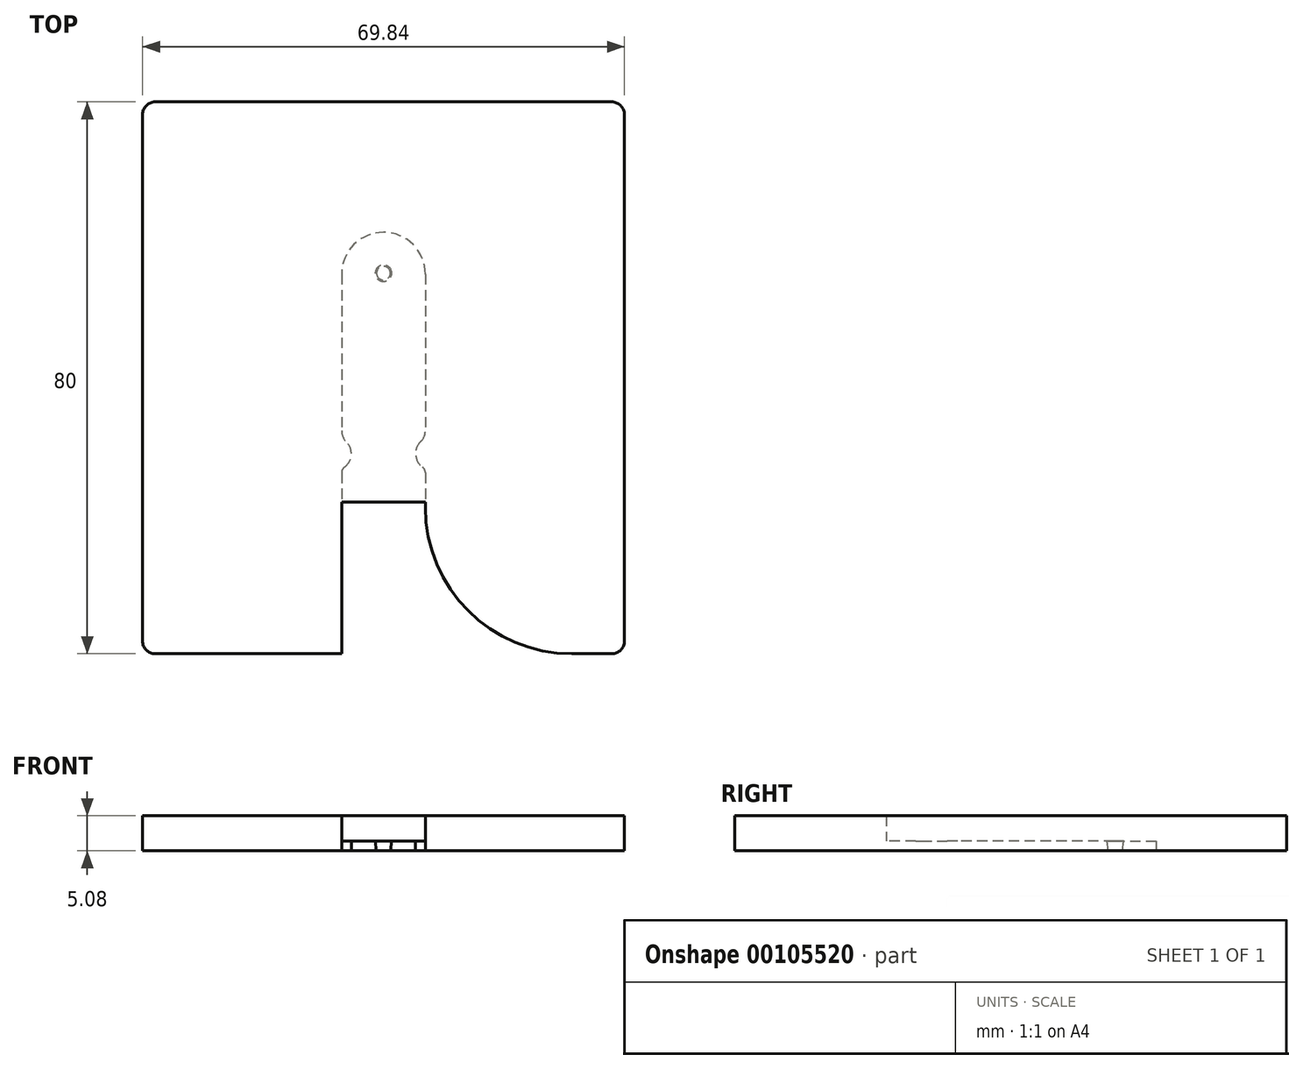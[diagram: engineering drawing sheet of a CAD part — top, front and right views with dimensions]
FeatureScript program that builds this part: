
annotation { "Feature Type Name" : "Feature", "Feature Type Description" : "" }
export const myFeature = defineFeature(function(context is Context, id is Id, definition is map)
    precondition{}
    {
        {
            var Q0;
            Q0=qCreatedBy(makeId("Top.planeOp"),FACE);
            var sketch = newSketch(context, id + "F0", { "sketchPlane" : qUnion([Q0])});
            skLineSegment(sketch, "E0.bottom", {"start": v(34.93, 40) * mm, "end": v(-34.93, 40) * mm});
            skLineSegment(sketch, "E0.top", {"start": v(34.93, -40) * mm, "end": v(-34.93, -40) * mm});
            skLineSegment(sketch, "E0.left", {"start": v(34.93, 40) * mm, "end": v(34.93, -40) * mm});
            skLineSegment(sketch, "E0.right", {"start": v(-34.93, 40) * mm, "end": v(-34.93, -40) * mm});
            skPoint(sketch, "E0.middle", {"position": v(0, 0) * mm});
            skSolve(sketch);
        }
        {
            var Q0;
            Q0 = qSketchRegion(id + "F0", true);
            extrude(context, id + "F1", {"entities" : qUnion([Q0]), "depth" : 5.08 * mm});
        }
        {
            var Q0;
            Q0=qCreatedBy(makeId("Top.planeOp"),FACE);
            var sketch = newSketch(context, id + "F2", { "sketchPlane" : qUnion([Q0])});
            skLineSegment(sketch, "E1", {"start": v(-44.66, 18.92) * mm, "end": v(-6.07, 18.92) * mm, "construction": true});
            skLineSegment(sketch, "E2.left", {"start": v(-6.07, 15.02) * mm, "end": v(-6.07, -3.94) * mm});
            skLineSegment(sketch, "E2.right", {"start": v(6.07, 15.02) * mm, "end": v(6.07, -3.94) * mm});
            skLineSegment(sketch, "E3", {"start": v(-6.07, -40.76) * mm, "end": v(6.07, -40.76) * mm});
            skLineSegment(sketch, "E4", {"start": v(-44, -1.4) * mm, "end": v(44.56, -1.4) * mm, "construction": true});
            skLineSegment(sketch, "E5.trimOffspring", {"start": v(-6.07, -3.94) * mm, "end": v(-6.07, -8.76) * mm});
            skLineSegment(sketch, "E6.trimOffspring", {"start": v(6.07, -3.94) * mm, "end": v(6.07, -8.76) * mm});
            skLineSegment(sketch, "E7", {"start": v(-50.47, -17.9) * mm, "end": v(45.13, -17.9) * mm, "construction": true});
            skLineSegment(sketch, "E8", {"start": v(-7.92, 15.62) * mm, "end": v(7.77, 15.62) * mm, "construction": true});
            skArc(sketch, "E9", {"start": v(6.07, -8.76) * mm, "mid": v(4.66, -10.98) * mm, "end": v(6.07, -13.2) * mm});
            skArc(sketch, "E10", {"start": v(-6.07, -13.2) * mm, "mid": v(-4.66, -10.98) * mm, "end": v(-6.07, -8.76) * mm});
            skArc(sketch, "E11", {"start": v(6.07, 15.02) * mm, "mid": v(0, 21.1) * mm, "end": v(-6.07, 15.02) * mm});
            skPoint(sketch, "E11.first.point", {"position": v(6.07, 15.02) * mm});
            skPoint(sketch, "E11.second.point", {"position": v(-6.07, 15.02) * mm});
            skPoint(sketch, "E11.third.point", {"position": v(0, 21.1) * mm});
            skPoint(sketch, "E12.1.internal.orphan", {"position": v(0, 21.92) * mm});
            skLineSegment(sketch, "E13.trimOffspring", {"start": v(6.07, 18.92) * mm, "end": v(44.03, 18.92) * mm, "construction": true});
            skLineSegment(sketch, "E14.trimOffspring", {"start": v(-6.07, -13.2) * mm, "end": v(-6.07, -17.9) * mm});
            skLineSegment(sketch, "E15.trimOffspring", {"start": v(6.07, -13.2) * mm, "end": v(6.07, -40.76) * mm});
            skLineSegment(sketch, "E16", {"start": v(-6.07, -17.9) * mm, "end": v(-6.07, -40.76) * mm});
            skSolve(sketch);
        }
        {
            var Q0;
            Q0 = qSketchRegion(id + "F2", true);
            extrude(context, id + "F3", {"entities" : qUnion([Q0]), "operationType" : NewBodyOperationType.REMOVE, "depth" : 1.4 * mm});
        }
        {
            var Q0;
            Q0=makeQuery(id+"F3.boolean.opBoolean","COPY",EDGE,{"derivedFrom":makeQuery(id+"F3.opExtrude","SWEPT_EDGE",EDGE,{"disambiguationData":[OSD([sQuery(id+"F2.wireOp",EDGE,"MfmMabNL-UIDS-KMx9-B42F-71vFicbcs6vO"),sQuery(id+"F2.wireOp",EDGE,"E15.trimOffspring")])]})});
            var Q1;
            Q1=makeQuery(id+"F3.boolean.opBoolean","COPY",EDGE,{"derivedFrom":makeQuery(id+"F3.opExtrude","SWEPT_EDGE",EDGE,{"disambiguationData":[OSD([sQuery(id+"F2.wireOp",EDGE,"d3NfdXWo-DDrf-wlvF-YYay-jeD352HhWQbW"),sQuery(id+"F2.wireOp",EDGE,"E14.trimOffspring")])]})});
            fillet(context, id + "F4", {"entities" : qUnion([Q0, Q1]), "radius" : 1 * mm, "tangentPropagation" : true, "allowEdgeOverflow" : false});
        }
        {
            var Q0;
            Q0=makeQuery(id+"F1.opExtrude","CAP_FACE",FACE,{"disambiguationData":[OSD([sQuery(id+"F0.wireOp",EDGE,"E0.bottom"),sQuery(id+"F0.wireOp",EDGE,"E0.top"),sQuery(id+"F0.wireOp",EDGE,"E0.left"),sQuery(id+"F0.wireOp",EDGE,"E0.right")])],"isStart":true});
            var sketch = newSketch(context, id + "F5", { "sketchPlane" : qUnion([Q0])});
            skLineSegment(sketch, "E17", {"start": v(4.06, -18.47) * mm, "end": v(-5.62, -18.47) * mm, "construction": true});
            skLineSegment(sketch, "E18", {"start": v(5.26, -15.17) * mm, "end": v(-3.7, -15.17) * mm, "construction": true});
            skCircle(sketch, "E19", {"center": v(0, -15.17) * mm, "radius": 1 * mm});
            skSolve(sketch);
        }
        {
            var Q0;
            Q0 = qSketchRegion(id + "F5", true);
            extrude(context, id + "F6", {"entities" : qUnion([Q0]), "operationType" : NewBodyOperationType.ADD, "endBound" : BoundingType.UP_TO_NEXT, "oppositeDirection" : true, "depth" : 25.4 * mm, "hasDraft" : true, "draftAngle" : 8 * degree});
        }
        {
            var Q0;
            Q0=makeQuery(id+"F3.boolean.opBoolean","COPY",FACE,{"derivedFrom":makeQuery(id+"F3.opExtrude","CAP_FACE",FACE,{"disambiguationData":[OSD([sQuery(id+"F2.wireOp",EDGE,"E2.bottom"),sQuery(id+"F2.wireOp",EDGE,"E2.left"),sQuery(id+"F2.wireOp",EDGE,"E2.right"),sQuery(id+"F2.wireOp",EDGE,"d3NfdXWo-DDrf-wlvF-YYay-jeD352HhWQbW"),sQuery(id+"F2.wireOp",EDGE,"E3"),sQuery(id+"F2.wireOp",EDGE,"MfmMabNL-UIDS-KMx9-B42F-71vFicbcs6vO"),sQuery(id+"F2.wireOp",EDGE,"1cVC2TSC-gZd2-qyUg-qrcc-GA4WCZSrXaVK"),sQuery(id+"F2.wireOp",EDGE,"QDqvuAkx-tC8D-Z4E2-XIwE-DFC6qE2ve7kV"),sQuery(id+"F2.wireOp",EDGE,"E5.trimOffspring"),sQuery(id+"F2.wireOp",EDGE,"E6.trimOffspring"),sQuery(id+"F2.wireOp",EDGE,"Lzuw7wu6-8RGA-Aa8n-5u6U-XDuzRWLJKQj1")])],"isStart":false})});
            var sketch = newSketch(context, id + "F7", { "sketchPlane" : qUnion([Q0])});
            skLineSegment(sketch, "E20", {"start": v(6.07, 18) * mm, "end": v(-6.07, 18) * mm});
            skLineSegment(sketch, "E21", {"start": v(-6.07, 18) * mm, "end": v(-6.07, 40) * mm});
            skLineSegment(sketch, "E22", {"start": v(6.07, 40) * mm, "end": v(-6.07, 40) * mm});
            skLineSegment(sketch, "E23", {"start": v(6.07, 18) * mm, "end": v(6.07, 40) * mm});
            skSolve(sketch);
        }
        {
            var Q0;
            Q0 = qSketchRegion(id + "F7", true);
            extrude(context, id + "F8", {"entities" : qUnion([Q0]), "operationType" : NewBodyOperationType.REMOVE, "endBound" : BoundingType.THROUGH_ALL, "oppositeDirection" : true, "depth" : 1.37 * mm});
        }
        {
            var Q0;
            Q0=makeQuery(id+"F1.opExtrude","SWEPT_EDGE",EDGE,{"disambiguationData":[OSD([sQuery(id+"F0.wireOp",EDGE,"E0.top"),sQuery(id+"F0.wireOp",EDGE,"E0.left")])]});
            var Q1;
            Q1=makeQuery(id+"F1.opExtrude","SWEPT_EDGE",EDGE,{"disambiguationData":[OSD([sQuery(id+"F0.wireOp",EDGE,"E0.top"),sQuery(id+"F0.wireOp",EDGE,"E0.right")])]});
            var Q2;
            Q2=makeQuery(id+"F1.opExtrude","SWEPT_EDGE",EDGE,{"disambiguationData":[OSD([sQuery(id+"F0.wireOp",EDGE,"E0.bottom"),sQuery(id+"F0.wireOp",EDGE,"E0.right")])]});
            var Q3;
            Q3=makeQuery(id+"F1.opExtrude","SWEPT_EDGE",EDGE,{"disambiguationData":[OSD([sQuery(id+"F0.wireOp",EDGE,"E0.bottom"),sQuery(id+"F0.wireOp",EDGE,"E0.left")])]});
            fillet(context, id + "F9", {"entities" : qUnion([Q0, Q1, Q2, Q3]), "radius" : 1.84 * mm, "tangentPropagation" : true, "allowEdgeOverflow" : false});
        }
        {
            var Q0;
            Q0=makeQuery(id+"F3.boolean.opBoolean","COPY",EDGE,{"derivedFrom":makeQuery(id+"F3.opExtrude","SWEPT_EDGE",EDGE,{"disambiguationData":[OSD([sQuery(id+"F2.wireOp",EDGE,"E9"),sQuery(id+"F2.wireOp",EDGE,"E15.trimOffspring")])]})});
            var Q1;
            Q1=makeQuery(id+"F3.boolean.opBoolean","COPY",EDGE,{"derivedFrom":makeQuery(id+"F3.opExtrude","SWEPT_EDGE",EDGE,{"disambiguationData":[OSD([sQuery(id+"F2.wireOp",EDGE,"E10"),sQuery(id+"F2.wireOp",EDGE,"E14.trimOffspring")])]})});
            var Q2;
            Q2=makeQuery(id+"F3.boolean.opBoolean","COPY",EDGE,{"derivedFrom":makeQuery(id+"F3.opExtrude","SWEPT_EDGE",EDGE,{"disambiguationData":[OSD([sQuery(id+"F2.wireOp",EDGE,"E6.trimOffspring"),sQuery(id+"F2.wireOp",EDGE,"E9")])]})});
            var Q3;
            Q3=makeQuery(id+"F3.boolean.opBoolean","COPY",EDGE,{"derivedFrom":makeQuery(id+"F3.opExtrude","SWEPT_EDGE",EDGE,{"disambiguationData":[OSD([sQuery(id+"F2.wireOp",EDGE,"E5.trimOffspring"),sQuery(id+"F2.wireOp",EDGE,"E10")])]})});
            fillet(context, id + "F10", {"entities" : qUnion([Q0, Q1, Q2, Q3]), "radius" : 2.1 * mm, "tangentPropagation" : true, "allowEdgeOverflow" : false});
        }
        {
            var Q0;
            Q0=makeQuery(id+"F8.boolean.opBoolean","MERGE",EDGE,{"derivedFrom":[makeQuery(id+"F3.boolean.opBoolean","INTERSECT",EDGE,{"derivedFrom":[makeQuery(id+"F1.opExtrude","SWEPT_FACE",FACE,{"disambiguationData":[OSD([sQuery(id+"F0.wireOp",EDGE,"E0.top")])]}),makeQuery(id+"F3.opExtrude","SWEPT_FACE",FACE,{"disambiguationData":[OSD([sQuery(id+"F2.wireOp",EDGE,"E15.trimOffspring")])]})]}),makeQuery(id+"F8.opExtrude","SWEPT_EDGE",EDGE,{"disambiguationData":[OSD([sQuery(id+"F7.wireOp",EDGE,"E23"),sQuery(id+"F7.wireOp",EDGE,"E22")])]})]});
            var Q1;
            Q1=makeQuery(id+"F8.boolean.opBoolean","MERGE",EDGE,{"derivedFrom":[makeQuery(id+"F3.boolean.opBoolean","INTERSECT",EDGE,{"derivedFrom":[makeQuery(id+"F1.opExtrude","SWEPT_FACE",FACE,{"disambiguationData":[OSD([sQuery(id+"F0.wireOp",EDGE,"E0.top")])]}),makeQuery(id+"F3.opExtrude","SWEPT_FACE",FACE,{"disambiguationData":[OSD([sQuery(id+"F2.wireOp",EDGE,"E14.trimOffspring"),sQuery(id+"F2.wireOp",EDGE,"E16")])]})]}),makeQuery(id+"F8.opExtrude","SWEPT_EDGE",EDGE,{"disambiguationData":[OSD([sQuery(id+"F7.wireOp",EDGE,"E21"),sQuery(id+"F7.wireOp",EDGE,"E22")])]})]});
            fillet(context, id + "F11", {"entities" : qUnion([Q0, Q1]), "radius" : 21.25 * mm, "tangentPropagation" : true, "allowEdgeOverflow" : false});
        }
    });
